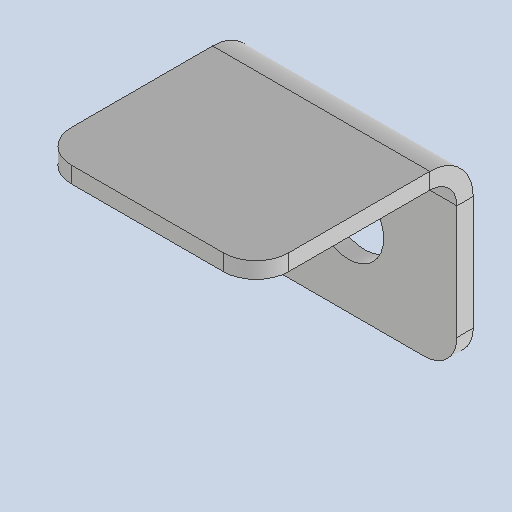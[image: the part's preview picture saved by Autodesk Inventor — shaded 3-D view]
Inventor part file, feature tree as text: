
AUTODESK INVENTOR PART (.ipt)
format: ipt  version: 2025 (Build 290162010, 162A)  size: 294,400 bytes
history: native  units: mm
features: sheet_metal_op x4, other x4, sketch x3, chamfer x1
ambient origin geometry x8: Origin, YZ Plane, XZ Plane, XY Plane, X Axis, Y Axis, Z Axis, Center Point
bodies: Body1 (feature_tree)
feature tree (12):
  sheet_metal_op  "Face2"
  sheet_metal_op  "Flange1"
  chamfer  "Corner Round6"
  sketch  "Sketch4"  dims[d36=40.0mm]
  other  "Plate2"
  sketch  "Sketch5"  dims[d37=35.0mm]
  sketch  "Sketch6"  dims[d38=3.0mm d40=15.0mm d41=13.0mm d42=3.0mm d43=0.0mm d44=3.0mm d45=1.5mm d46=6.0mm d47=5.0mm d48=40.0mm d49=90.0deg d50=5.0mm d51=12.0mm d52=3.0mm d53=5.0mm d54=6.0mm]
  other  "Plate3"
  sheet_metal_op  "Bend1"
  sheet_metal_op  "Corner1"
  other  "Cut1"
  other  "Definition1"
